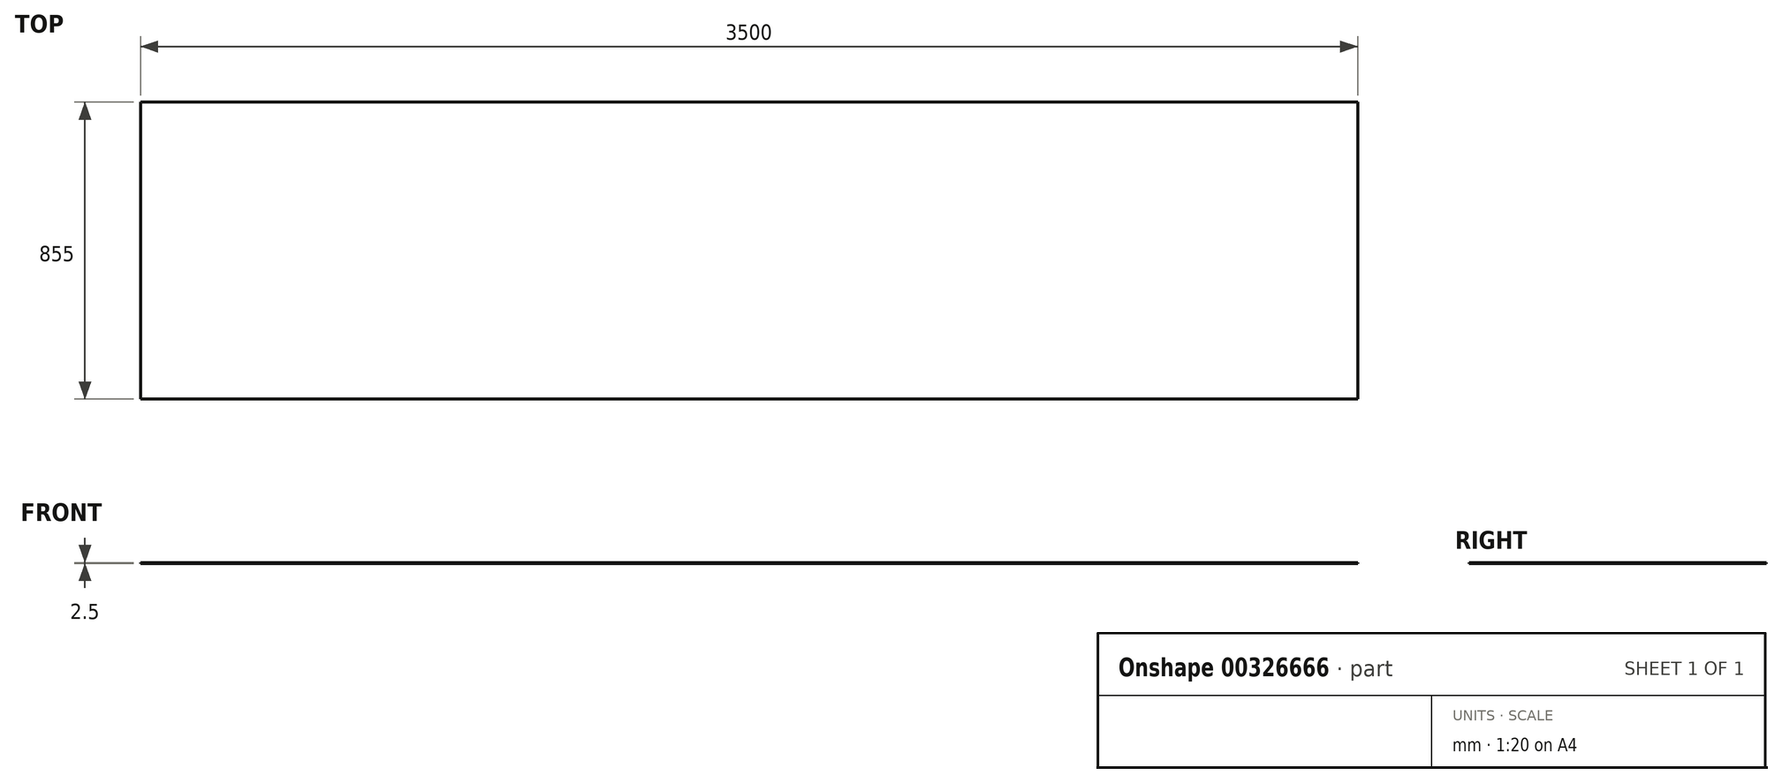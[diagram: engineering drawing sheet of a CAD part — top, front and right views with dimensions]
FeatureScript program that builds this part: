
annotation { "Feature Type Name" : "Feature", "Feature Type Description" : "" }
export const myFeature = defineFeature(function(context is Context, id is Id, definition is map)
    precondition{}
    {
        {
            var Q0;
            Q0=qCreatedBy(makeId("Top.planeOp"),FACE);
            var sketch = newSketch(context, id + "F0", { "sketchPlane" : qUnion([Q0])});
            skLineSegment(sketch, "E0.bottom", {"start": v(0, 0) * mm, "end": v(3500, 0) * mm});
            skLineSegment(sketch, "E0.top", {"start": v(0, 855) * mm, "end": v(3500, 855) * mm});
            skLineSegment(sketch, "E0.left", {"start": v(0, 0) * mm, "end": v(0, 855) * mm});
            skLineSegment(sketch, "E0.right", {"start": v(3500, 0) * mm, "end": v(3500, 855) * mm});
            skSolve(sketch);
        }
        {
            var Q0;
            Q0=makeQuery(id+"F0.imprint","IMPRINT",FACE,{"disambiguationData":[TD([[makeQuery(id+"F0.imprint","IMPRINT",EDGE,{"derivedFrom":sQuery(id+"F0.wireOp",EDGE,"E0.bottom")}),1.0]])]});
            extrude(context, id + "F1", {"entities" : qUnion([Q0]), "depth" : 2.5 * mm});
        }
    });
